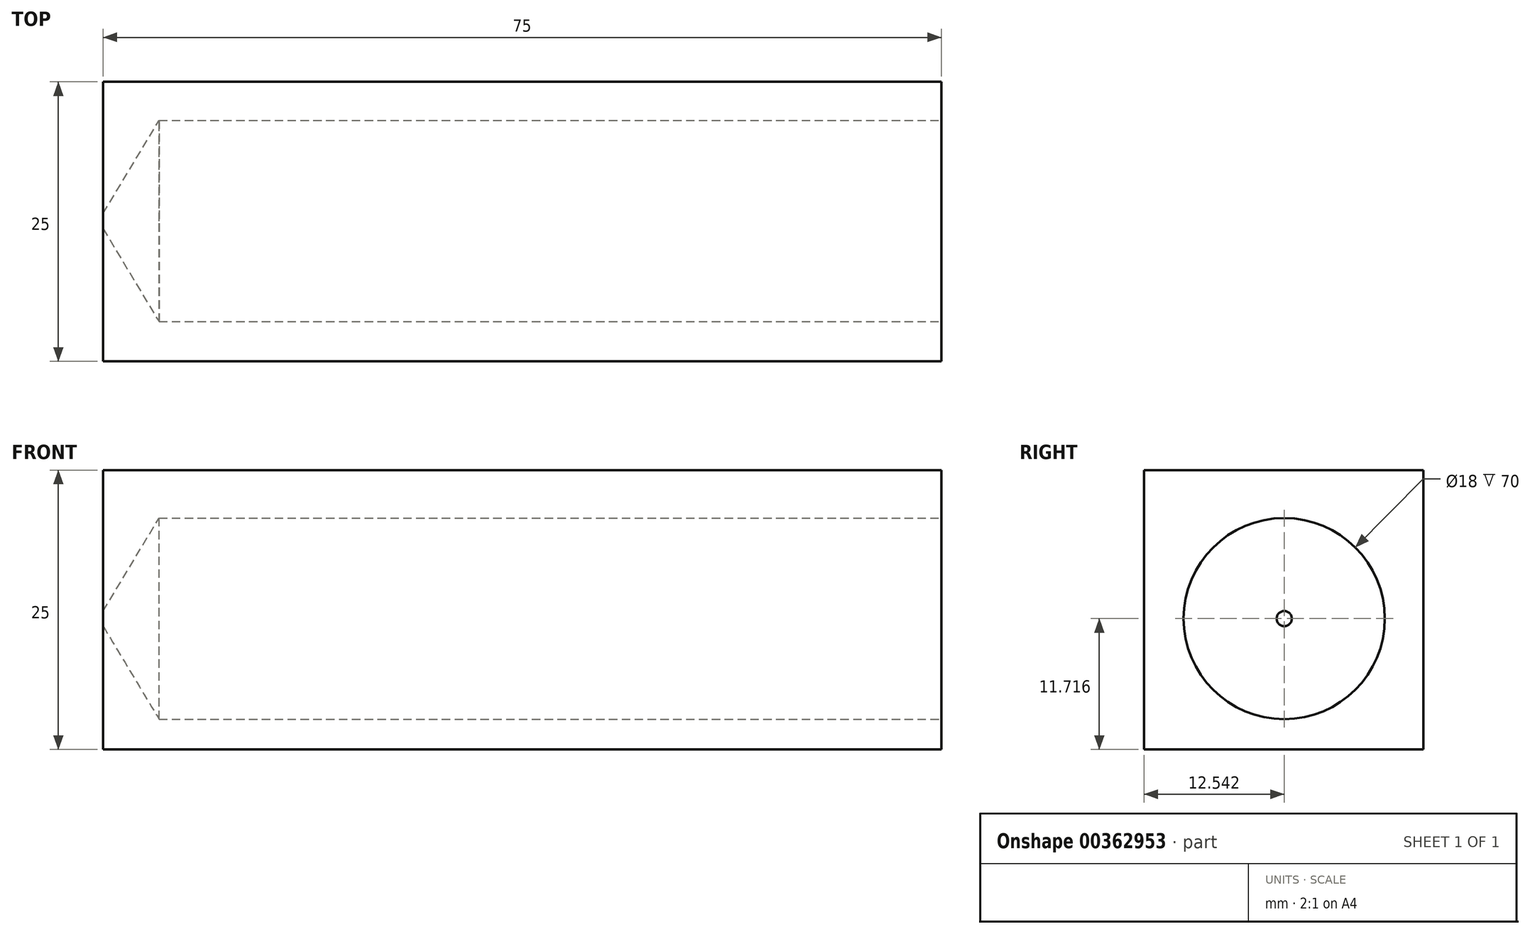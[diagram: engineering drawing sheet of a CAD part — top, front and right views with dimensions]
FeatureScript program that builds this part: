
annotation { "Feature Type Name" : "Feature", "Feature Type Description" : "" }
export const myFeature = defineFeature(function(context is Context, id is Id, definition is map)
    precondition{}
    {
        {
            var Q0;
            Q0=qCreatedBy(makeId("Front.planeOp"),FACE);
            var sketch = newSketch(context, id + "F0", { "sketchPlane" : qUnion([Q0])});
            skLineSegment(sketch, "E0.bottom", {"start": v(56.36, 25) * mm, "end": v(-18.64, 25) * mm});
            skLineSegment(sketch, "E0.top", {"start": v(56.36, 0) * mm, "end": v(-18.64, 0) * mm});
            skLineSegment(sketch, "E0.left", {"start": v(56.36, 25) * mm, "end": v(56.36, 0) * mm});
            skLineSegment(sketch, "E0.right", {"start": v(-18.64, 25) * mm, "end": v(-18.64, 0) * mm});
            skSolve(sketch);
        }
        {
            var Q0;
            Q0=makeQuery(id+"F0.imprint","IMPRINT",FACE,{"disambiguationData":[TD([[makeQuery(id+"F0.imprint","IMPRINT",EDGE,{"derivedFrom":sQuery(id+"F0.wireOp",EDGE,"E0.bottom")}),1.0]])]});
            extrude(context, id + "F1", {"entities" : qUnion([Q0]), "depth" : 25 * mm});
        }
        {
            var Q0;
            Q0=makeQuery(id+"F1.opExtrude","SWEPT_FACE",FACE,{"disambiguationData":[OSD([sQuery(id+"F0.wireOp",EDGE,"E0.left")])]});
            var sketch = newSketch(context, id + "F2", { "sketchPlane" : qUnion([Q0])});
            skCircle(sketch, "E1", {"center": v(-12.46, 11.72) * mm, "radius": 4.54 * mm});
            skSolve(sketch);
        }
        {
            var Q0;
            Q0=sQuery(id+"F2.wireOp",VERTEX,"E1.center");
            var Q1;
            Q1=makeQuery(id+"F1.opExtrude","SWEPT_BODY",BODY,{"disambiguationData":[OSD([sQuery(id+"F0.wireOp",EDGE,"E0.bottom"),sQuery(id+"F0.wireOp",EDGE,"E0.top"),sQuery(id+"F0.wireOp",EDGE,"E0.left"),sQuery(id+"F0.wireOp",EDGE,"E0.right")])]});
            hole(context, id + "F3", {"style" : HoleStyle.SIMPLE, "endStyle" : HoleEndStyle.BLIND, "holeDiameter" : 18 * mm, "holeDepth" : 70 * mm, "isTappedThrough" : true, "tappedDepth" : 12 * mm, "tapClearance" : 3, "locations" : qUnion([Q0]), "scope" : qUnion([Q1])});
        }
    });
